# Revit family: Indoor_Pendant Lamp_Santa&Cole_Tekiò Horizontal
name_source: partatom
category: Luminarias
revit_build: Autodesk Revit 2018 (Build: 20190510_1515(x64)
units: mm (PartAtom-declared; Revit-internal decimal feet)

## family parameters
Anfitrión = Cara
Compartido = No
Corte con vacíos al cargar = No
Cota de conector redondo = Diámetro de uso
Origen de luz = Sí
Punto de cálculo de habitación = No
Tipo de pieza = Normal

## types (4) — shared parameters
Assembly Instructions - CE = https://www.santacole.com
Assembly Instructions - UL = https://www.santacole.com
Cambio de temperatura de color de luz atenuada = <Ninguno>
Elevación por defecto = 1219 mm
Energy Label = https://www.santacole.com
Fabricante = Santa & Cole
Filtro de color = 16777215
Lampshade Material = Santa&Cole - Washi Japanese Paper
Manufacturer website = http://www.santacole.com
Modelo = Tekiò Horizontal
Structure Material = Santa&Cole - White Matte Finish
Technical Information = https://www.santacole.com
URL = https://www.santacole.com
Visibility_P1 = Sí
Voltaje (90-305 V) = 220 V
Ángulo de inclinación = -90.00°

## per-type parameters (varying)
| type | Archivo de red fotométrica | Carga aparente | Code | Light Source Height | Load | Longitud de línea de emisión | V1 | V2 | V3 | Visibility_P2 | Visibility_P3 | Visibility_P4 |
| Tekiò Horizontal P1 | TEKIO HORIZONTAL P1.IES | 43 W | TEKHE1+TEKHP1+TEKF01/TEKF03 | 264 mm | 43 W | 525 mm | Sí | No | No | No | No | No |
| Tekiò Horizontal P2 | TEKIO HORITZONTAL P2.IES | 73 W | TEKHE2+TEKHP2+TEKF01/TEKF03 | 525 mm | 73 W | 1049 mm | No | Sí | No | Sí | No | No |
| Tekiò Horizontal P3 | TEKIO HORIZONTAL P3.IES | 100 W | TEKHE3+TEKHP3+TEKF01/TEKF03 | 791 mm | 100 W | 1579 mm | No | No | Sí | Sí | Sí | No |
| Tekiò Horizontal P4 | TEKIO HORIZONTAL P4.IES | 120 W | TEKHE4+TEKHP4+TEKF01/TEKF03 | 1054 mm  [stored 3.45801 ft] | 120 W | 2106 mm  [stored 6.90945 ft] | No | No | No | Sí | Sí | Sí |

note: [stored X ft] marks values corroborated as IEEE doubles in the binary element streams (Revit-internal decimal feet)

## geometry (parser evidence)
native form markers: Blend x4, Sweep x3
no freeform markers — native parametric forms only
